FCSTD DOCUMENT  (FreeCAD 0.17R13217 (Git))
Label: 07-triangulo-isosceles
License: All rights reserved
LicenseURL: http://en.wikipedia.org/wiki/All_rights_reserved
objects: Sketcher::SketchObject×1, PartDesign::Body×1
note: 2 computed .brp shape members not serialized (recipe doc carries the construction recipe); baked Part::Feature solids carry a one-line shape summary decoded from their .brp

FEATURE [Sketcher::SketchObject] Sketch
  MapMode = 5
  Support = -> [XY_Plane]
  sketch-geometry (4):
    g0: LineSegment StartX=-35.1543 StartY=0 StartZ=0 EndX=-17.5772 EndY=17.5772 EndZ=0
    g1: LineSegment StartX=-17.5772 StartY=17.5772 StartZ=0 EndX=0 EndY=0 EndZ=0
    g2: LineSegment StartX=0 StartY=0 StartZ=0 EndX=-35.1543 EndY=0 EndZ=0
    g3: LineSegment [constr] StartX=-17.5772 StartY=17.5772 StartZ=0 EndX=-17.5772 EndY=0 EndZ=0
  constraints (10):
    c: Coincident(g0,g1)
    c: Coincident(g1,g2)
    c: Coincident(g2,g0)
    c: Horizontal(g2)
    c: Equal(g0,g1)
    c: Coincident(g1,g-1)
    c: Coincident(g3,g0)
    c: PointOnObject(g3,g2)
    c: Vertical(g3)
    c: Angle(g3,g1) = 0.785398
FEATURE [PartDesign::Body] Body
  Group = -> [Sketch]
  Origin = -> Origin
